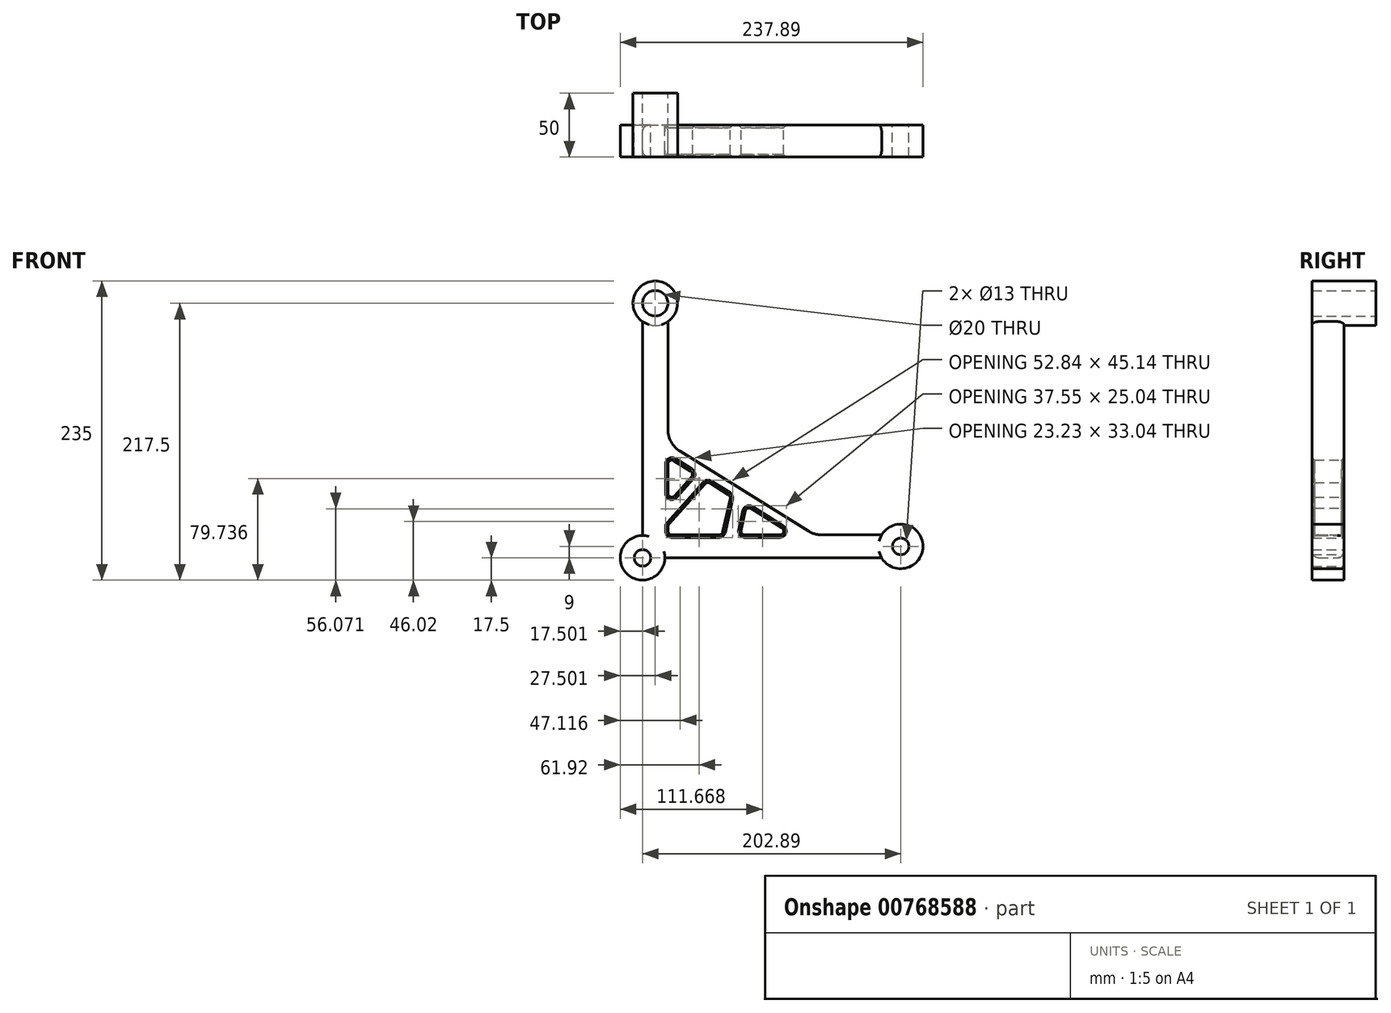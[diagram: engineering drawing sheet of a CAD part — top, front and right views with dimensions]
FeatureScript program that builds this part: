
annotation { "Feature Type Name" : "Feature", "Feature Type Description" : "" }
export const myFeature = defineFeature(function(context is Context, id is Id, definition is map)
    precondition{}
    {
        {
            var Q0;
            Q0=qCreatedBy(makeId("Front.planeOp"),FACE);
            var sketch = newSketch(context, id + "F0", { "sketchPlane" : qUnion([Q0])});
            skLineSegment(sketch, "E0", {"start": v(-117.2, 185.64) * mm, "end": v(-117.2, 17.5) * mm});
            skLineSegment(sketch, "E1", {"start": v(-99.7, 0) * mm, "end": v(70.67, 0) * mm});
            skLineSegment(sketch, "E2", {"start": v(70.67, 18) * mm, "end": v(23.75, 18) * mm});
            skLineSegment(sketch, "E3", {"start": v(13.2, 21) * mm, "end": v(-87.76, 83.71) * mm});
            skLineSegment(sketch, "E4", {"start": v(-97.2, 100.7) * mm, "end": v(-97.2, 185.64) * mm});
            skLineSegment(sketch, "E5", {"start": v(-92.63, 76.3) * mm, "end": v(-79.38, 68.08) * mm});
            skLineSegment(sketch, "E6", {"start": v(-9.26, 18) * mm, "end": v(-36.82, 18) * mm});
            skLineSegment(sketch, "E7", {"start": v(-97.2, 21) * mm, "end": v(-97.2, 24.4) * mm});
            skLineSegment(sketch, "E8", {"start": v(-78.73, 63.53) * mm, "end": v(-91.97, 48.7) * mm});
            skLineSegment(sketch, "E9", {"start": v(-36.43, 36.7) * mm, "end": v(-39.75, 21.65) * mm});
            skLineSegment(sketch, "E10", {"start": v(-68.09, 58.14) * mm, "end": v(-96.45, 26.4) * mm});
            skLineSegment(sketch, "E11", {"start": v(-48.43, 46.5) * mm, "end": v(-54.2, 20.35) * mm});
            skLineSegment(sketch, "E12.trimOffspring", {"start": v(-97.2, 50.7) * mm, "end": v(-97.2, 73.76) * mm});
            skLineSegment(sketch, "E13.trimOffspring", {"start": v(-64.27, 58.7) * mm, "end": v(-49.78, 49.7) * mm});
            skLineSegment(sketch, "E14.trimOffspring", {"start": v(-57.12, 18) * mm, "end": v(-94.2, 18) * mm});
            skLineSegment(sketch, "E15.trimOffspring", {"start": v(-31.92, 38.6) * mm, "end": v(-7.68, 23.55) * mm});
            skPoint(sketch, "E16.visualSharp", {"position": v(-97.2, 89.58) * mm});
            skArc(sketch, "E16.filletArc", {"start": v(-97.2, 100.7) * mm, "mid": v(-94.69, 90.98) * mm, "end": v(-87.76, 83.71) * mm});
            skPoint(sketch, "E17.visualSharp", {"position": v(18.05, 18) * mm});
            skArc(sketch, "E17.filletArc", {"start": v(13.2, 21) * mm, "mid": v(18.27, 18.77) * mm, "end": v(23.75, 18) * mm});
            skPoint(sketch, "E18.visualSharp", {"position": v(-97.2, 79.15) * mm});
            skArc(sketch, "E18.filletArc", {"start": v(-92.63, 76.3) * mm, "mid": v(-95.67, 76.38) * mm, "end": v(-97.2, 73.76) * mm});
            skPoint(sketch, "E19.visualSharp", {"position": v(-97.2, 42.84) * mm});
            skArc(sketch, "E19.filletArc", {"start": v(-97.2, 50.7) * mm, "mid": v(-95.28, 47.9) * mm, "end": v(-91.97, 48.7) * mm});
            skPoint(sketch, "E20.visualSharp", {"position": v(-76.35, 66.2) * mm});
            skArc(sketch, "E20.filletArc", {"start": v(-78.73, 63.53) * mm, "mid": v(-78, 65.96) * mm, "end": v(-79.38, 68.08) * mm});
            skPoint(sketch, "E21.visualSharp", {"position": v(-66.4, 60.02) * mm});
            skArc(sketch, "E21.filletArc", {"start": v(-64.27, 58.7) * mm, "mid": v(-66.28, 59.11) * mm, "end": v(-68.09, 58.14) * mm});
            skPoint(sketch, "E22.visualSharp", {"position": v(-47.98, 48.58) * mm});
            skArc(sketch, "E22.filletArc", {"start": v(-48.43, 46.5) * mm, "mid": v(-48.6, 48.31) * mm, "end": v(-49.78, 49.7) * mm});
            skPoint(sketch, "E23.visualSharp", {"position": v(-54.71, 18) * mm});
            skArc(sketch, "E23.filletArc", {"start": v(-57.12, 18) * mm, "mid": v(-55.24, 18.66) * mm, "end": v(-54.2, 20.35) * mm});
            skPoint(sketch, "E24.visualSharp", {"position": v(-97.2, 18) * mm});
            skArc(sketch, "E24.filletArc", {"start": v(-97.2, 21) * mm, "mid": v(-96.33, 18.88) * mm, "end": v(-94.2, 18) * mm});
            skPoint(sketch, "E25.visualSharp", {"position": v(-97.2, 25.54) * mm});
            skArc(sketch, "E25.filletArc", {"start": v(-96.45, 26.4) * mm, "mid": v(-97.01, 25.47) * mm, "end": v(-97.2, 24.4) * mm});
            skPoint(sketch, "E26.visualSharp", {"position": v(-35.52, 40.84) * mm});
            skArc(sketch, "E26.filletArc", {"start": v(-31.92, 38.6) * mm, "mid": v(-34.67, 38.82) * mm, "end": v(-36.43, 36.7) * mm});
            skPoint(sketch, "E27.visualSharp", {"position": v(-40.55, 18) * mm});
            skArc(sketch, "E27.filletArc", {"start": v(-39.75, 21.65) * mm, "mid": v(-39.16, 19.12) * mm, "end": v(-36.82, 18) * mm});
            skPoint(sketch, "E28.visualSharp", {"position": v(1.26, 18) * mm});
            skArc(sketch, "E28.filletArc", {"start": v(-9.26, 18) * mm, "mid": v(-6.37, 20.18) * mm, "end": v(-7.68, 23.55) * mm});
            skPoint(sketch, "E29.visualSharp", {"position": v(-117.2, 0) * mm});
            skArc(sketch, "E30", {"start": v(-97.2, 185.64) * mm, "mid": v(-107.2, 217.5) * mm, "end": v(-117.2, 185.64) * mm});
            skArc(sketch, "E31", {"start": v(70.67, 0) * mm, "mid": v(103.18, 9) * mm, "end": v(70.67, 18) * mm});
            skArc(sketch, "E32", {"start": v(-117.2, 17.5) * mm, "mid": v(-129.58, -12.37) * mm, "end": v(-99.7, 0) * mm});
            skCircle(sketch, "E33", {"center": v(-107.2, 200) * mm, "radius": 6.5 * mm});
            skCircle(sketch, "E34", {"center": v(-117.2, 0) * mm, "radius": 6.5 * mm});
            skCircle(sketch, "E35", {"center": v(85.68, 9) * mm, "radius": 6.5 * mm});
            skSolve(sketch);
        }
        {
            var Q0;
            Q0=makeQuery(id+"F0.imprint","IMPRINT",FACE,{"disambiguationData":[TD([[makeQuery(id+"F0.imprint","IMPRINT",EDGE,{"derivedFrom":sQuery(id+"F0.wireOp",EDGE,"E0")}),1.0]])]});
            extrude(context, id + "F1", {"entities" : qUnion([Q0]), "depth" : 25 * mm, "offsetDistance" : 25 * mm});
        }
        {
            var Q0;
            Q0=makeQuery(id+"F1.opExtrude","CAP_EDGE",EDGE,{"disambiguationData":[OSD([sQuery(id+"F0.wireOp",EDGE,"E4")])],"isStart":false});
            var Q1;
            Q1=makeQuery(id+"F1.opExtrude","CAP_EDGE",EDGE,{"disambiguationData":[OSD([sQuery(id+"F0.wireOp",EDGE,"E0")])],"isStart":false});
            var Q2;
            Q2=makeQuery(id+"F1.opExtrude","CAP_EDGE",EDGE,{"disambiguationData":[OSD([sQuery(id+"F0.wireOp",EDGE,"E1")])],"isStart":false});
            var Q3;
            Q3=makeQuery(id+"F1.opExtrude","CAP_EDGE",EDGE,{"disambiguationData":[OSD([sQuery(id+"F0.wireOp",EDGE,"E0")])],"isStart":true});
            var Q4;
            Q4=makeQuery(id+"F1.opExtrude","CAP_EDGE",EDGE,{"disambiguationData":[OSD([sQuery(id+"F0.wireOp",EDGE,"E4")])],"isStart":true});
            var Q5;
            Q5=makeQuery(id+"F1.opExtrude","CAP_EDGE",EDGE,{"disambiguationData":[OSD([sQuery(id+"F0.wireOp",EDGE,"E1")])],"isStart":true});
            fillet(context, id + "F2", {"entities" : qUnion([Q0, Q1, Q2, Q3, Q4, Q5]), "radius" : 5 * mm, "tangentPropagation" : true, "allowEdgeOverflow" : false});
        }
        {
            var Q0;
            Q0=qCreatedBy(makeId("Front.planeOp"),FACE);
            var sketch = newSketch(context, id + "F3", { "sketchPlane" : qUnion([Q0])});
            skCircle(sketch, "E36", {"center": v(-107.2, 200) * mm, "radius": 17.5 * mm});
            skSolve(sketch);
        }
        {
            var Q0;
            Q0 = qSketchRegion(id + "F3", true);
            extrude(context, id + "F4", {"entities" : qUnion([Q0]), "operationType" : NewBodyOperationType.ADD, "oppositeDirection" : true, "depth" : 25 * mm, "offsetDistance" : 25 * mm});
        }
        {
            var Q0;
            Q0=sQuery(id+"F0.wireOp",VERTEX,"E30.center");
            var Q1;
            Q1=makeQuery(id+"F1.opExtrude","SWEPT_BODY",BODY,{"disambiguationData":[OSD([sQuery(id+"F0.wireOp",EDGE,"E0"),sQuery(id+"F0.wireOp",EDGE,"E1"),sQuery(id+"F0.wireOp",EDGE,"E2"),sQuery(id+"F0.wireOp",EDGE,"E3"),sQuery(id+"F0.wireOp",EDGE,"E4"),sQuery(id+"F0.wireOp",EDGE,"E5"),sQuery(id+"F0.wireOp",EDGE,"E6"),sQuery(id+"F0.wireOp",EDGE,"E7"),sQuery(id+"F0.wireOp",EDGE,"E8"),sQuery(id+"F0.wireOp",EDGE,"E9"),sQuery(id+"F0.wireOp",EDGE,"E10"),sQuery(id+"F0.wireOp",EDGE,"E11"),sQuery(id+"F0.wireOp",EDGE,"E12.trimOffspring"),sQuery(id+"F0.wireOp",EDGE,"E13.trimOffspring"),sQuery(id+"F0.wireOp",EDGE,"E14.trimOffspring"),sQuery(id+"F0.wireOp",EDGE,"E15.trimOffspring"),sQuery(id+"F0.wireOp",EDGE,"E16.filletArc"),sQuery(id+"F0.wireOp",EDGE,"E17.filletArc"),sQuery(id+"F0.wireOp",EDGE,"E18.filletArc"),sQuery(id+"F0.wireOp",EDGE,"E19.filletArc"),sQuery(id+"F0.wireOp",EDGE,"E20.filletArc"),sQuery(id+"F0.wireOp",EDGE,"E21.filletArc"),sQuery(id+"F0.wireOp",EDGE,"E22.filletArc"),sQuery(id+"F0.wireOp",EDGE,"E23.filletArc"),sQuery(id+"F0.wireOp",EDGE,"E24.filletArc"),sQuery(id+"F0.wireOp",EDGE,"E25.filletArc"),sQuery(id+"F0.wireOp",EDGE,"E26.filletArc"),sQuery(id+"F0.wireOp",EDGE,"E27.filletArc"),sQuery(id+"F0.wireOp",EDGE,"E28.filletArc"),sQuery(id+"F0.wireOp",EDGE,"E30"),sQuery(id+"F0.wireOp",EDGE,"E31"),sQuery(id+"F0.wireOp",EDGE,"E32"),sQuery(id+"F0.wireOp",EDGE,"E33"),sQuery(id+"F0.wireOp",EDGE,"E34"),sQuery(id+"F0.wireOp",EDGE,"E35")])]});
            hole(context, id + "F5", {"style" : HoleStyle.SIMPLE, "endStyle" : HoleEndStyle.THROUGH, "holeDiameter" : 20 * mm, "majorDiameter" : 5 * mm, "isTappedThrough" : true, "tappedDepth" : 12 * mm, "tapClearance" : 3, "locations" : qUnion([Q0]), "scope" : qUnion([Q1])});
        }
        {
            var Q0;
            Q0=makeQuery(id+"F1.opExtrude","CAP_EDGE",EDGE,{"disambiguationData":[OSD([sQuery(id+"F0.wireOp",EDGE,"E18.filletArc")])],"isStart":false});
            var Q1;
            Q1=makeQuery(id+"F1.opExtrude","CAP_EDGE",EDGE,{"disambiguationData":[OSD([sQuery(id+"F0.wireOp",EDGE,"E5")])],"isStart":false});
            var Q2;
            Q2=makeQuery(id+"F1.opExtrude","CAP_EDGE",EDGE,{"disambiguationData":[OSD([sQuery(id+"F0.wireOp",EDGE,"E20.filletArc")])],"isStart":false});
            var Q3;
            Q3=makeQuery(id+"F1.opExtrude","CAP_EDGE",EDGE,{"disambiguationData":[OSD([sQuery(id+"F0.wireOp",EDGE,"E8")])],"isStart":false});
            var Q4;
            Q4=makeQuery(id+"F1.opExtrude","CAP_EDGE",EDGE,{"disambiguationData":[OSD([sQuery(id+"F0.wireOp",EDGE,"E19.filletArc")])],"isStart":false});
            var Q5;
            Q5=makeQuery(id+"F1.opExtrude","CAP_EDGE",EDGE,{"disambiguationData":[OSD([sQuery(id+"F0.wireOp",EDGE,"E12.trimOffspring")])],"isStart":false});
            var Q6;
            Q6=makeQuery(id+"F1.opExtrude","CAP_EDGE",EDGE,{"disambiguationData":[OSD([sQuery(id+"F0.wireOp",EDGE,"E13.trimOffspring")])],"isStart":false});
            var Q7;
            Q7=makeQuery(id+"F1.opExtrude","CAP_EDGE",EDGE,{"disambiguationData":[OSD([sQuery(id+"F0.wireOp",EDGE,"E22.filletArc")])],"isStart":false});
            var Q8;
            Q8=makeQuery(id+"F1.opExtrude","CAP_EDGE",EDGE,{"disambiguationData":[OSD([sQuery(id+"F0.wireOp",EDGE,"E11")])],"isStart":false});
            var Q9;
            Q9=makeQuery(id+"F1.opExtrude","CAP_EDGE",EDGE,{"disambiguationData":[OSD([sQuery(id+"F0.wireOp",EDGE,"E6")])],"isStart":false});
            chamfer(context, id + "F6", {"entities" : qUnion([Q0, Q1, Q2, Q3, Q4, Q5, Q6, Q7, Q8, Q9]), "width" : 2 * mm, "tangentPropagation" : true});
        }
        {
            var Q0;
            Q0=makeQuery(id+"F1.opExtrude","CAP_EDGE",EDGE,{"disambiguationData":[OSD([sQuery(id+"F0.wireOp",EDGE,"E27.filletArc")])],"isStart":true});
            var Q1;
            Q1=makeQuery(id+"F1.opExtrude","CAP_EDGE",EDGE,{"disambiguationData":[OSD([sQuery(id+"F0.wireOp",EDGE,"E14.trimOffspring")])],"isStart":true});
            var Q2;
            Q2=makeQuery(id+"F1.opExtrude","CAP_EDGE",EDGE,{"disambiguationData":[OSD([sQuery(id+"F0.wireOp",EDGE,"E12.trimOffspring")])],"isStart":true});
            chamfer(context, id + "F7", {"entities" : qUnion([Q0, Q1, Q2]), "width" : 2 * mm, "tangentPropagation" : true});
        }
    });
